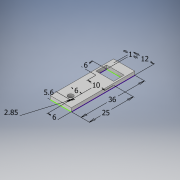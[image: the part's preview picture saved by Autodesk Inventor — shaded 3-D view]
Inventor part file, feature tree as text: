
AUTODESK INVENTOR PART (.ipt)
format: ipt  version: 2019.4 (Build 234330000, 330)  size: 112,128 bytes
history: native  units: mm
features: extrude x1, sketch x1
ambient origin geometry x8: Origin, YZ Plane, XZ Plane, XY Plane, X Axis, Y Axis, Z Axis, Center Point
bodies: Solid1 (feature_tree)
feature tree (2):
  extrude  "Extrusion1"  Depth=36.0mm
  sketch  "Sketch1"  dims[d0=2.85mm d1=36.0mm d2=10.0mm d3=1.0mm d4=6.0mm d5=12.0mm d6=6.0mm d8=5.6mm d9=25.0mm d11=6.0mm d12=2.0mm d13=0.0mm]
